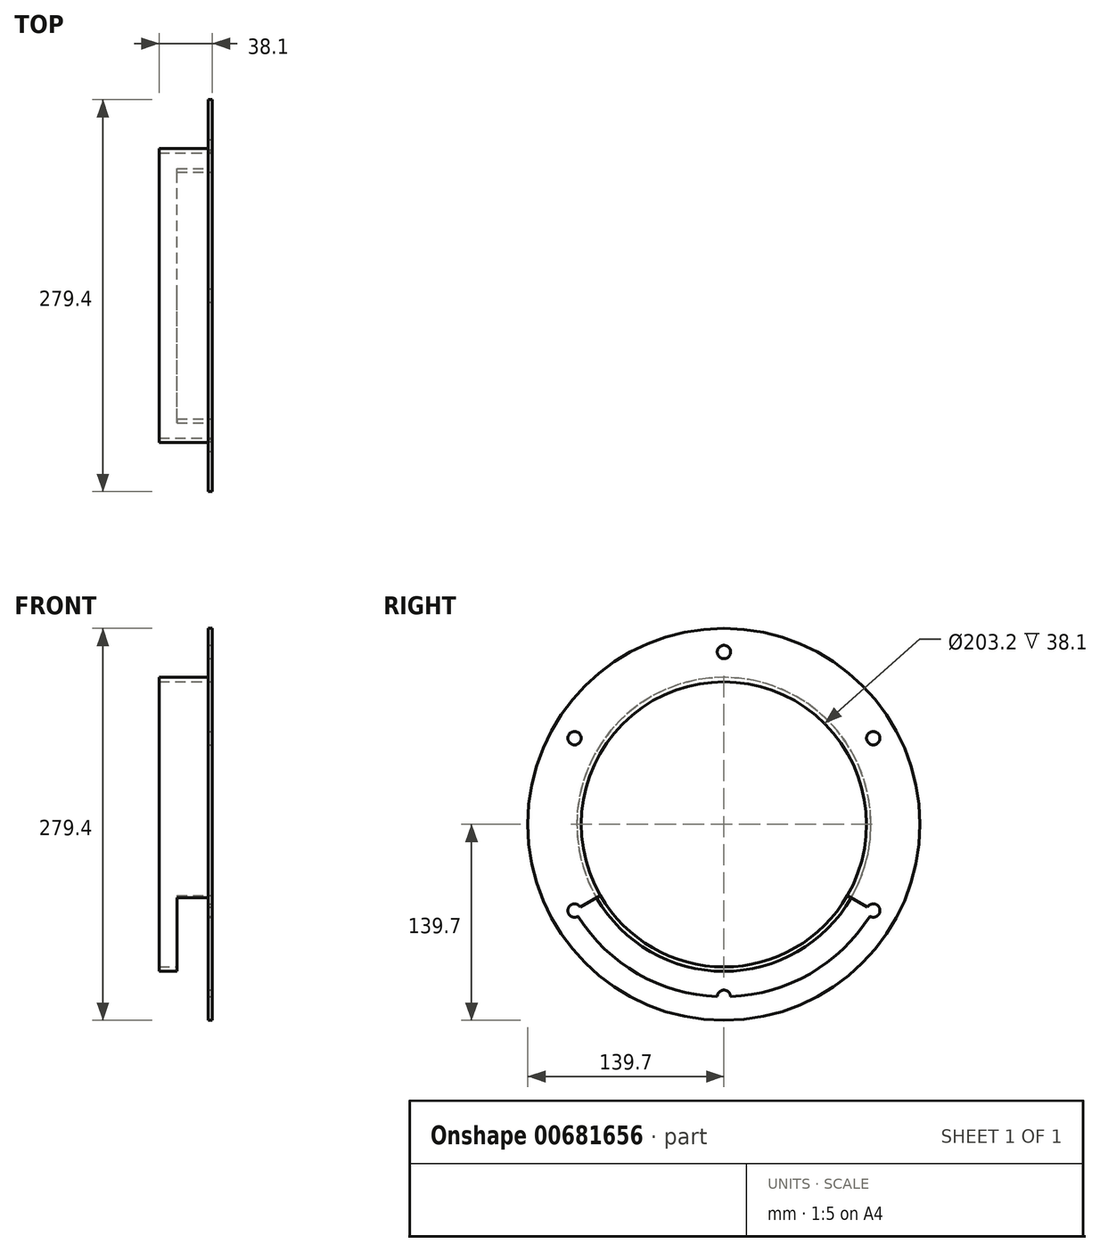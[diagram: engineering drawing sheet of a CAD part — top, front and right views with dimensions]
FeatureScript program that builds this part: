
annotation { "Feature Type Name" : "Feature", "Feature Type Description" : "" }
export const myFeature = defineFeature(function(context is Context, id is Id, definition is map)
    precondition{}
    {
        {
            var Q0;
            Q0=qCreatedBy(makeId("Front.planeOp"),FACE);
            var sketch = newSketch(context, id + "F0", { "sketchPlane" : qUnion([Q0])});
            skLineSegment(sketch, "E0", {"start": v(0, 0) * mm, "end": v(0, 101.6) * mm, "construction": true});
            skLineSegment(sketch, "E1", {"start": v(0, 101.6) * mm, "end": v(-38.1, 101.6) * mm});
            skLineSegment(sketch, "E2", {"start": v(-38.1, 101.6) * mm, "end": v(-38.1, 104.78) * mm});
            skLineSegment(sketch, "E3", {"start": v(-38.1, 104.78) * mm, "end": v(-3.17, 104.78) * mm});
            skLineSegment(sketch, "E4", {"start": v(-3.17, 104.78) * mm, "end": v(-3.17, 139.7) * mm});
            skLineSegment(sketch, "E5", {"start": v(-3.17, 139.7) * mm, "end": v(0, 139.7) * mm});
            skLineSegment(sketch, "E6", {"start": v(0, 139.7) * mm, "end": v(0, 101.6) * mm});
            skLineSegment(sketch, "E7", {"start": v(0, 0) * mm, "end": v(-81.36, 0) * mm, "construction": true});
            skSolve(sketch);
        }
        {
            var Q0;
            Q0=makeQuery(id+"F0.imprint","IMPRINT",FACE,{"disambiguationData":[TD([[makeQuery(id+"F0.imprint","IMPRINT",EDGE,{"derivedFrom":sQuery(id+"F0.wireOp",EDGE,"E1")}),-1.0]])]});
            var Q1;
            Q1=sQuery(id+"F0.wireOp",EDGE,"E7");
            revolve(context, id + "F1", {"surfaceOperationType" : NewSurfaceOperationType.NEW, "entities" : qUnion([Q0]), "axis" : qUnion([Q1]), "revolveType" : RevolveType.FULL});
        }
        {
            var Q0;
            Q0=qCreatedBy(makeId("Right.planeOp"),FACE);
            var sketch = newSketch(context, id + "F2", { "sketchPlane" : qUnion([Q0])});
            skCircle(sketch, "E8", {"center": v(0, 0) * mm, "radius": 122.87 * mm});
            skLineSegment(sketch, "E9", {"start": v(0, 0) * mm, "end": v(0, 143.34) * mm});
            skLineSegment(sketch, "E10", {"start": v(0, 0) * mm, "end": v(0, -143.34) * mm});
            skLineSegment(sketch, "E11", {"start": v(0, 0) * mm, "end": v(133.74, 77.21) * mm});
            skLineSegment(sketch, "E12", {"start": v(0, 0) * mm, "end": v(136.7, -78.93) * mm});
            skLineSegment(sketch, "E13.MirrorCS", {"start": v(0, 0) * mm, "end": v(-133.74, 77.21) * mm});
            skLineSegment(sketch, "E14.MirrorCS", {"start": v(0, 0) * mm, "end": v(-136.7, -78.93) * mm});
            skCircle(sketch, "E15", {"center": v(-106.41, -61.44) * mm, "radius": 4.76 * mm});
            skCircle(sketch, "E16", {"center": v(-106.41, 61.44) * mm, "radius": 4.76 * mm});
            skCircle(sketch, "E17", {"center": v(0, 122.87) * mm, "radius": 4.76 * mm});
            skCircle(sketch, "E18", {"center": v(106.41, 61.44) * mm, "radius": 4.76 * mm});
            skCircle(sketch, "E19", {"center": v(106.41, -61.44) * mm, "radius": 4.76 * mm});
            skCircle(sketch, "E20", {"center": v(0, -122.87) * mm, "radius": 4.76 * mm});
            skSolve(sketch);
        }
        {
            var Q0;
            {var subQ0=sQuery(id+"F2.wireOp",EDGE,"E16");var subQ1=sQuery(id+"F2.wireOp",EDGE,"E8");var subQ2=makeQuery(id+"F2.imprint","INTERSECT",VERTEX,{"disambiguationData":[OD(0.0)],"derivedFrom":[subQ1,subQ0]});Q0=makeQuery(id+"F2.imprint","IMPRINT",FACE,{"disambiguationData":[TD([[makeQuery(id+"F2.imprint","IMPRINT",EDGE,{"disambiguationData":[TD([[subQ2,-1.0]])],"derivedFrom":subQ1}),-1.0]])]});}
            var Q1;
            {var subQ0=sQuery(id+"F2.wireOp",EDGE,"E16");var subQ1=sQuery(id+"F2.wireOp",EDGE,"E8");var subQ2=makeQuery(id+"F2.imprint","INTERSECT",VERTEX,{"disambiguationData":[OD(1.0)],"derivedFrom":[subQ1,subQ0]});Q1=makeQuery(id+"F2.imprint","IMPRINT",FACE,{"disambiguationData":[TD([[makeQuery(id+"F2.imprint","IMPRINT",EDGE,{"disambiguationData":[TD([[subQ2,1.0]])],"derivedFrom":subQ1}),-1.0]])]});}
            var Q2;
            {var subQ0=sQuery(id+"F2.wireOp",EDGE,"E16");var subQ1=sQuery(id+"F2.wireOp",EDGE,"E8");var subQ2=makeQuery(id+"F2.imprint","INTERSECT",VERTEX,{"disambiguationData":[OD(1.0)],"derivedFrom":[subQ1,subQ0]});Q2=makeQuery(id+"F2.imprint","IMPRINT",FACE,{"disambiguationData":[TD([[makeQuery(id+"F2.imprint","IMPRINT",EDGE,{"disambiguationData":[TD([[subQ2,1.0]])],"derivedFrom":subQ1}),1.0]])]});}
            var Q3;
            {var subQ0=sQuery(id+"F2.wireOp",EDGE,"E16");var subQ1=sQuery(id+"F2.wireOp",EDGE,"E8");var subQ2=makeQuery(id+"F2.imprint","INTERSECT",VERTEX,{"disambiguationData":[OD(0.0)],"derivedFrom":[subQ1,subQ0]});Q3=makeQuery(id+"F2.imprint","IMPRINT",FACE,{"disambiguationData":[TD([[makeQuery(id+"F2.imprint","IMPRINT",EDGE,{"disambiguationData":[TD([[subQ2,-1.0]])],"derivedFrom":subQ1}),1.0]])]});}
            var Q4;
            {var subQ0=sQuery(id+"F2.wireOp",EDGE,"E15");var subQ1=sQuery(id+"F2.wireOp",EDGE,"E8");var subQ2=makeQuery(id+"F2.imprint","INTERSECT",VERTEX,{"disambiguationData":[OD(0.0)],"derivedFrom":[subQ1,subQ0]});Q4=makeQuery(id+"F2.imprint","IMPRINT",FACE,{"disambiguationData":[TD([[makeQuery(id+"F2.imprint","IMPRINT",EDGE,{"disambiguationData":[TD([[subQ2,-1.0]])],"derivedFrom":subQ1}),-1.0]])]});}
            var Q5;
            {var subQ0=sQuery(id+"F2.wireOp",EDGE,"E15");var subQ1=sQuery(id+"F2.wireOp",EDGE,"E8");var subQ2=makeQuery(id+"F2.imprint","INTERSECT",VERTEX,{"disambiguationData":[OD(0.0)],"derivedFrom":[subQ1,subQ0]});Q5=makeQuery(id+"F2.imprint","IMPRINT",FACE,{"disambiguationData":[TD([[makeQuery(id+"F2.imprint","IMPRINT",EDGE,{"disambiguationData":[TD([[subQ2,-1.0]])],"derivedFrom":subQ1}),1.0]])]});}
            var Q6;
            {var subQ0=sQuery(id+"F2.wireOp",EDGE,"E15");var subQ1=sQuery(id+"F2.wireOp",EDGE,"E8");var subQ2=makeQuery(id+"F2.imprint","INTERSECT",VERTEX,{"disambiguationData":[OD(1.0)],"derivedFrom":[subQ1,subQ0]});Q6=makeQuery(id+"F2.imprint","IMPRINT",FACE,{"disambiguationData":[TD([[makeQuery(id+"F2.imprint","IMPRINT",EDGE,{"disambiguationData":[TD([[subQ2,1.0]])],"derivedFrom":subQ1}),1.0]])]});}
            var Q7;
            {var subQ0=sQuery(id+"F2.wireOp",EDGE,"E15");var subQ1=sQuery(id+"F2.wireOp",EDGE,"E8");var subQ2=makeQuery(id+"F2.imprint","INTERSECT",VERTEX,{"disambiguationData":[OD(1.0)],"derivedFrom":[subQ1,subQ0]});Q7=makeQuery(id+"F2.imprint","IMPRINT",FACE,{"disambiguationData":[TD([[makeQuery(id+"F2.imprint","IMPRINT",EDGE,{"disambiguationData":[TD([[subQ2,1.0]])],"derivedFrom":subQ1}),-1.0]])]});}
            var Q8;
            {var subQ0=sQuery(id+"F2.wireOp",EDGE,"E20");var subQ1=sQuery(id+"F2.wireOp",EDGE,"E8");var subQ2=makeQuery(id+"F2.imprint","INTERSECT",VERTEX,{"disambiguationData":[OD(1.0)],"derivedFrom":[subQ1,subQ0]});Q8=makeQuery(id+"F2.imprint","IMPRINT",FACE,{"disambiguationData":[TD([[makeQuery(id+"F2.imprint","IMPRINT",EDGE,{"disambiguationData":[TD([[subQ2,1.0]])],"derivedFrom":subQ1}),-1.0]])]});}
            var Q9;
            {var subQ0=sQuery(id+"F2.wireOp",EDGE,"E20");var subQ1=sQuery(id+"F2.wireOp",EDGE,"E8");var subQ2=makeQuery(id+"F2.imprint","INTERSECT",VERTEX,{"disambiguationData":[OD(1.0)],"derivedFrom":[subQ1,subQ0]});Q9=makeQuery(id+"F2.imprint","IMPRINT",FACE,{"disambiguationData":[TD([[makeQuery(id+"F2.imprint","IMPRINT",EDGE,{"disambiguationData":[TD([[subQ2,1.0]])],"derivedFrom":subQ1}),1.0]])]});}
            var Q10;
            {var subQ0=sQuery(id+"F2.wireOp",EDGE,"E20");var subQ1=sQuery(id+"F2.wireOp",EDGE,"E8");var subQ2=makeQuery(id+"F2.imprint","INTERSECT",VERTEX,{"disambiguationData":[OD(0.0)],"derivedFrom":[subQ1,subQ0]});Q10=makeQuery(id+"F2.imprint","IMPRINT",FACE,{"disambiguationData":[TD([[makeQuery(id+"F2.imprint","IMPRINT",EDGE,{"disambiguationData":[TD([[subQ2,-1.0]])],"derivedFrom":subQ1}),1.0]])]});}
            var Q11;
            {var subQ0=sQuery(id+"F2.wireOp",EDGE,"E20");var subQ1=sQuery(id+"F2.wireOp",EDGE,"E8");var subQ2=makeQuery(id+"F2.imprint","INTERSECT",VERTEX,{"disambiguationData":[OD(0.0)],"derivedFrom":[subQ1,subQ0]});Q11=makeQuery(id+"F2.imprint","IMPRINT",FACE,{"disambiguationData":[TD([[makeQuery(id+"F2.imprint","IMPRINT",EDGE,{"disambiguationData":[TD([[subQ2,-1.0]])],"derivedFrom":subQ1}),-1.0]])]});}
            var Q12;
            {var subQ0=sQuery(id+"F2.wireOp",EDGE,"E19");var subQ1=sQuery(id+"F2.wireOp",EDGE,"E8");var subQ2=makeQuery(id+"F2.imprint","INTERSECT",VERTEX,{"disambiguationData":[OD(1.0)],"derivedFrom":[subQ1,subQ0]});Q12=makeQuery(id+"F2.imprint","IMPRINT",FACE,{"disambiguationData":[TD([[makeQuery(id+"F2.imprint","IMPRINT",EDGE,{"disambiguationData":[TD([[subQ2,1.0]])],"derivedFrom":subQ1}),1.0]])]});}
            var Q13;
            {var subQ0=sQuery(id+"F2.wireOp",EDGE,"E19");var subQ1=sQuery(id+"F2.wireOp",EDGE,"E8");var subQ2=makeQuery(id+"F2.imprint","INTERSECT",VERTEX,{"disambiguationData":[OD(1.0)],"derivedFrom":[subQ1,subQ0]});Q13=makeQuery(id+"F2.imprint","IMPRINT",FACE,{"disambiguationData":[TD([[makeQuery(id+"F2.imprint","IMPRINT",EDGE,{"disambiguationData":[TD([[subQ2,1.0]])],"derivedFrom":subQ1}),-1.0]])]});}
            var Q14;
            {var subQ0=sQuery(id+"F2.wireOp",EDGE,"E19");var subQ1=sQuery(id+"F2.wireOp",EDGE,"E8");var subQ2=makeQuery(id+"F2.imprint","INTERSECT",VERTEX,{"disambiguationData":[OD(0.0)],"derivedFrom":[subQ1,subQ0]});Q14=makeQuery(id+"F2.imprint","IMPRINT",FACE,{"disambiguationData":[TD([[makeQuery(id+"F2.imprint","IMPRINT",EDGE,{"disambiguationData":[TD([[subQ2,-1.0]])],"derivedFrom":subQ1}),-1.0]])]});}
            var Q15;
            {var subQ0=sQuery(id+"F2.wireOp",EDGE,"E19");var subQ1=sQuery(id+"F2.wireOp",EDGE,"E8");var subQ2=makeQuery(id+"F2.imprint","INTERSECT",VERTEX,{"disambiguationData":[OD(0.0)],"derivedFrom":[subQ1,subQ0]});Q15=makeQuery(id+"F2.imprint","IMPRINT",FACE,{"disambiguationData":[TD([[makeQuery(id+"F2.imprint","IMPRINT",EDGE,{"disambiguationData":[TD([[subQ2,-1.0]])],"derivedFrom":subQ1}),1.0]])]});}
            var Q16;
            {var subQ0=sQuery(id+"F2.wireOp",EDGE,"E18");var subQ1=sQuery(id+"F2.wireOp",EDGE,"E8");var subQ2=makeQuery(id+"F2.imprint","INTERSECT",VERTEX,{"disambiguationData":[OD(1.0)],"derivedFrom":[subQ1,subQ0]});Q16=makeQuery(id+"F2.imprint","IMPRINT",FACE,{"disambiguationData":[TD([[makeQuery(id+"F2.imprint","IMPRINT",EDGE,{"disambiguationData":[TD([[subQ2,1.0]])],"derivedFrom":subQ1}),-1.0]])]});}
            var Q17;
            {var subQ0=sQuery(id+"F2.wireOp",EDGE,"E18");var subQ1=sQuery(id+"F2.wireOp",EDGE,"E8");var subQ2=makeQuery(id+"F2.imprint","INTERSECT",VERTEX,{"disambiguationData":[OD(0.0)],"derivedFrom":[subQ1,subQ0]});Q17=makeQuery(id+"F2.imprint","IMPRINT",FACE,{"disambiguationData":[TD([[makeQuery(id+"F2.imprint","IMPRINT",EDGE,{"disambiguationData":[TD([[subQ2,-1.0]])],"derivedFrom":subQ1}),-1.0]])]});}
            var Q18;
            {var subQ0=sQuery(id+"F2.wireOp",EDGE,"E18");var subQ1=sQuery(id+"F2.wireOp",EDGE,"E8");var subQ2=makeQuery(id+"F2.imprint","INTERSECT",VERTEX,{"disambiguationData":[OD(0.0)],"derivedFrom":[subQ1,subQ0]});Q18=makeQuery(id+"F2.imprint","IMPRINT",FACE,{"disambiguationData":[TD([[makeQuery(id+"F2.imprint","IMPRINT",EDGE,{"disambiguationData":[TD([[subQ2,-1.0]])],"derivedFrom":subQ1}),1.0]])]});}
            var Q19;
            {var subQ0=sQuery(id+"F2.wireOp",EDGE,"E18");var subQ1=sQuery(id+"F2.wireOp",EDGE,"E8");var subQ2=makeQuery(id+"F2.imprint","INTERSECT",VERTEX,{"disambiguationData":[OD(1.0)],"derivedFrom":[subQ1,subQ0]});Q19=makeQuery(id+"F2.imprint","IMPRINT",FACE,{"disambiguationData":[TD([[makeQuery(id+"F2.imprint","IMPRINT",EDGE,{"disambiguationData":[TD([[subQ2,1.0]])],"derivedFrom":subQ1}),1.0]])]});}
            var Q20;
            {var subQ0=sQuery(id+"F2.wireOp",EDGE,"E17");var subQ1=sQuery(id+"F2.wireOp",EDGE,"E8");var subQ2=makeQuery(id+"F2.imprint","INTERSECT",VERTEX,{"disambiguationData":[OD(0.0)],"derivedFrom":[subQ1,subQ0]});Q20=makeQuery(id+"F2.imprint","IMPRINT",FACE,{"disambiguationData":[TD([[makeQuery(id+"F2.imprint","IMPRINT",EDGE,{"disambiguationData":[TD([[subQ2,-1.0]])],"derivedFrom":subQ1}),-1.0]])]});}
            var Q21;
            {var subQ0=sQuery(id+"F2.wireOp",EDGE,"E17");var subQ1=sQuery(id+"F2.wireOp",EDGE,"E8");var subQ2=makeQuery(id+"F2.imprint","INTERSECT",VERTEX,{"disambiguationData":[OD(1.0)],"derivedFrom":[subQ1,subQ0]});Q21=makeQuery(id+"F2.imprint","IMPRINT",FACE,{"disambiguationData":[TD([[makeQuery(id+"F2.imprint","IMPRINT",EDGE,{"disambiguationData":[TD([[subQ2,1.0]])],"derivedFrom":subQ1}),-1.0]])]});}
            var Q22;
            {var subQ0=sQuery(id+"F2.wireOp",EDGE,"E17");var subQ1=sQuery(id+"F2.wireOp",EDGE,"E8");var subQ2=makeQuery(id+"F2.imprint","INTERSECT",VERTEX,{"disambiguationData":[OD(1.0)],"derivedFrom":[subQ1,subQ0]});Q22=makeQuery(id+"F2.imprint","IMPRINT",FACE,{"disambiguationData":[TD([[makeQuery(id+"F2.imprint","IMPRINT",EDGE,{"disambiguationData":[TD([[subQ2,1.0]])],"derivedFrom":subQ1}),1.0]])]});}
            var Q23;
            {var subQ0=sQuery(id+"F2.wireOp",EDGE,"E17");var subQ1=sQuery(id+"F2.wireOp",EDGE,"E8");var subQ2=makeQuery(id+"F2.imprint","INTERSECT",VERTEX,{"disambiguationData":[OD(0.0)],"derivedFrom":[subQ1,subQ0]});Q23=makeQuery(id+"F2.imprint","IMPRINT",FACE,{"disambiguationData":[TD([[makeQuery(id+"F2.imprint","IMPRINT",EDGE,{"disambiguationData":[TD([[subQ2,-1.0]])],"derivedFrom":subQ1}),1.0]])]});}
            var Q24;
            Q24=sQuery(id+"F2.wireOp",EDGE,"E16");
            var Q25;
            Q25=sQuery(id+"F2.wireOp",EDGE,"E15");
            var Q26;
            Q26=sQuery(id+"F2.wireOp",EDGE,"E20");
            var Q27;
            Q27=sQuery(id+"F2.wireOp",EDGE,"E19");
            var Q28;
            Q28=sQuery(id+"F2.wireOp",EDGE,"E18");
            var Q29;
            Q29=sQuery(id+"F2.wireOp",EDGE,"E17");
            extrude(context, id + "F3", {"entities" : qUnion([Q0, Q1, Q2, Q3, Q4, Q5, Q6, Q7, Q8, Q9, Q10, Q11, Q12, Q13, Q14, Q15, Q16, Q17, Q18, Q19, Q20, Q21, Q22, Q23]), "operationType" : NewBodyOperationType.REMOVE, "surfaceEntities" : qUnion([Q24, Q25, Q26, Q27, Q28, Q29]), "oppositeDirection" : true, "depth" : 25.4 * mm, "offsetDistance" : 25.4 * mm});
        }
    });
